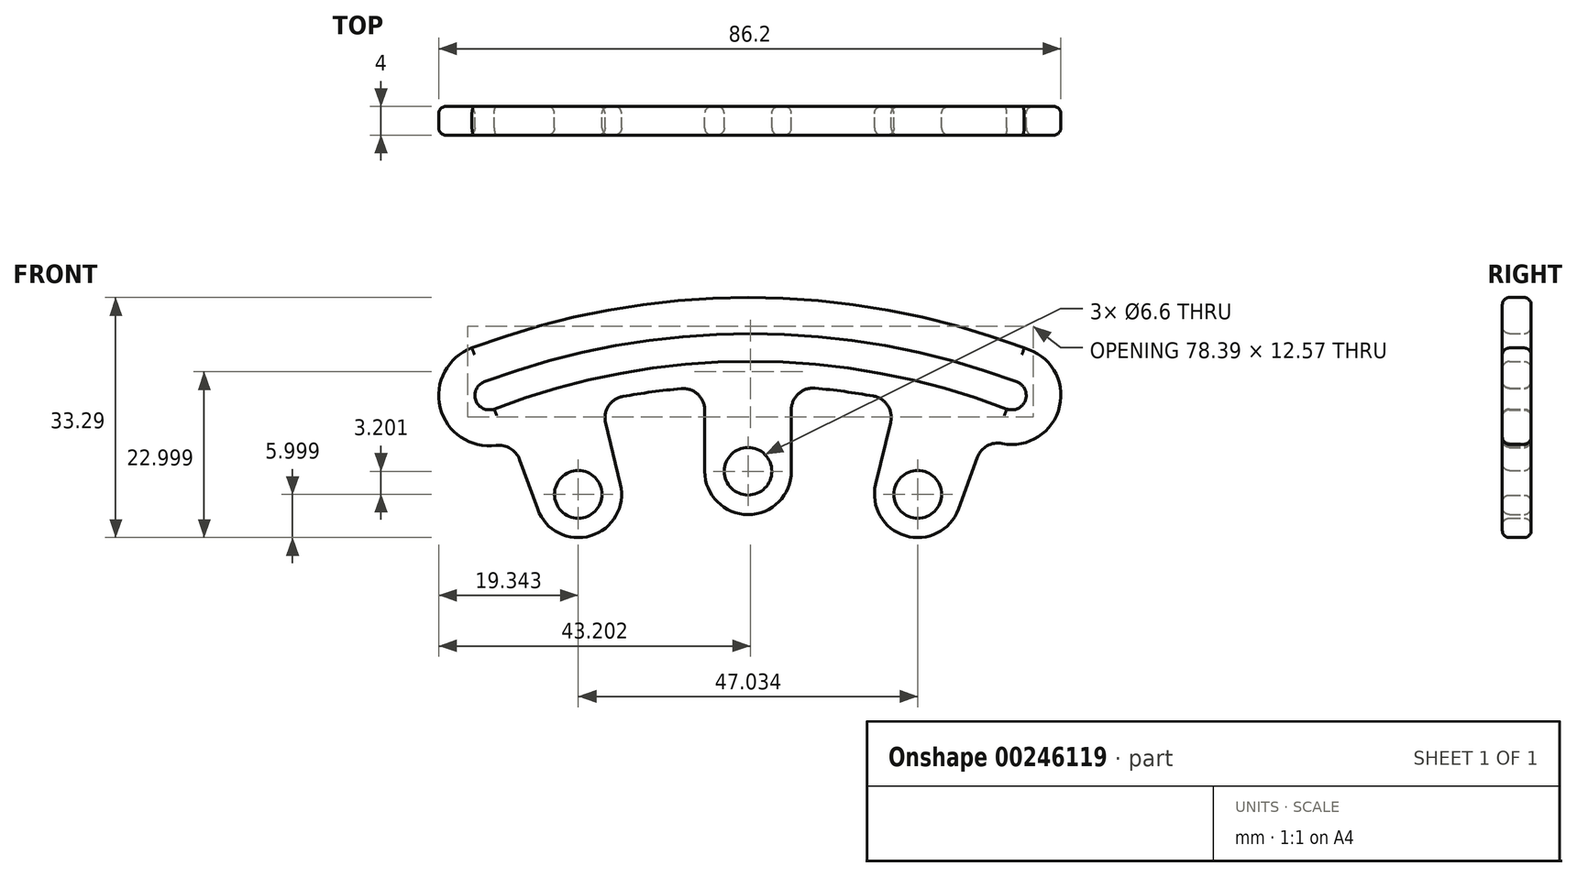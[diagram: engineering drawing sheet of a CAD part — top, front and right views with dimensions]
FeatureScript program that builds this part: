
annotation { "Feature Type Name" : "Feature", "Feature Type Description" : "" }
export const myFeature = defineFeature(function(context is Context, id is Id, definition is map)
    precondition{}
    {
        {
            var Q0;
            Q0=qCreatedBy(makeId("Front.planeOp"),FACE);
            var sketch = newSketch(context, id + "F0", { "sketchPlane" : qUnion([Q0])});
            skLineSegment(sketch, "E0", {"start": v(0, 0) * mm, "end": v(0, 189.24) * mm, "construction": true});
            skCircle(sketch, "E1", {"center": v(0, 88) * mm, "radius": 3.3 * mm});
            skCircle(sketch, "E2", {"center": v(23.52, 84.8) * mm, "radius": 3.3 * mm});
            skCircle(sketch, "E3", {"center": v(-23.52, 84.8) * mm, "radius": 3.3 * mm});
            skLineSegment(sketch, "E4", {"start": v(0, 0) * mm, "end": v(23.52, 84.8) * mm, "construction": true});
            skLineSegment(sketch, "E5", {"start": v(0, 0) * mm, "end": v(-23.52, 84.8) * mm, "construction": true});
            skArc(sketch, "E6", {"start": v(23.52, 84.8) * mm, "mid": v(0, 88) * mm, "end": v(-23.52, 84.8) * mm, "construction": true});
            skCircle(sketch, "E7", {"center": v(-23.52, 84.8) * mm, "radius": 6 * mm, "construction": true});
            skCircle(sketch, "E8", {"center": v(0, 88) * mm, "radius": 6 * mm, "construction": true});
            skCircle(sketch, "E9", {"center": v(23.52, 84.8) * mm, "radius": 6 * mm, "construction": true});
            skLineSegment(sketch, "E10", {"start": v(-23.52, 84.8) * mm, "end": v(23.52, 84.8) * mm, "construction": true});
            skLineSegment(sketch, "E11", {"start": v(-23.52, 84.8) * mm, "end": v(-17.68, 86.2) * mm, "construction": true});
            skLineSegment(sketch, "E12", {"start": v(0, 88) * mm, "end": v(69.3, 88) * mm, "construction": true});
            skLineSegment(sketch, "E13", {"start": v(69.3, 88) * mm, "end": v(69.3, 0) * mm, "construction": true});
            skLineSegment(sketch, "E14", {"start": v(0, 88) * mm, "end": v(6, 88) * mm, "construction": true});
            skLineSegment(sketch, "E15", {"start": v(6, 88) * mm, "end": v(6, 96.53) * mm});
            skLineSegment(sketch, "E16", {"start": v(0, 88) * mm, "end": v(-6, 88) * mm, "construction": true});
            skLineSegment(sketch, "E17", {"start": v(-6, 88) * mm, "end": v(-6, 96.47) * mm});
            skLineSegment(sketch, "E18", {"start": v(-23.52, 84.8) * mm, "end": v(-17.52, 84.8) * mm});
            skLineSegment(sketch, "E19", {"start": v(-17.68, 86.2) * mm, "end": v(-19.73, 94.72) * mm});
            skLineSegment(sketch, "E20", {"start": v(23.52, 84.8) * mm, "end": v(17.68, 86.2) * mm});
            skLineSegment(sketch, "E21", {"start": v(17.68, 86.2) * mm, "end": v(19.75, 94.78) * mm});
            skLineSegment(sketch, "E22", {"start": v(-35.17, 96.63) * mm, "end": v(35.86, 96.63) * mm, "construction": true});
            skArc(sketch, "E23", {"start": v(35.86, 96.63) * mm, "mid": v(0.34, 103.22) * mm, "end": v(-35.17, 96.63) * mm});
            skArc(sketch, "E24", {"start": v(-36.54, 100.4) * mm, "mid": v(-37.74, 97.83) * mm, "end": v(-35.17, 96.63) * mm});
            skArc(sketch, "E25", {"start": v(35.86, 96.63) * mm, "mid": v(38.42, 97.83) * mm, "end": v(37.22, 100.4) * mm});
            skArc(sketch, "E26", {"start": v(37.22, 100.4) * mm, "mid": v(0.34, 107.08) * mm, "end": v(-36.54, 100.4) * mm});
            skCircle(sketch, "E27", {"center": v(-35.86, 98.51) * mm, "radius": 3 * mm, "construction": true});
            skCircle(sketch, "E28", {"center": v(36.54, 98.51) * mm, "radius": 3 * mm, "construction": true});
            skLineSegment(sketch, "E29", {"start": v(-36.88, 101.33) * mm, "end": v(37.57, 101.33) * mm, "construction": true});
            skLineSegment(sketch, "E30", {"start": v(37.57, 101.33) * mm, "end": v(35.51, 95.7) * mm, "construction": true});
            skLineSegment(sketch, "E31", {"start": v(35.51, 95.7) * mm, "end": v(-34.83, 95.7) * mm, "construction": true});
            skArc(sketch, "E32", {"start": v(36.54, 98.51) * mm, "mid": v(0.34, 105.05) * mm, "end": v(-35.86, 98.51) * mm, "construction": true});
            skLineSegment(sketch, "E33", {"start": v(-38.25, 105.1) * mm, "end": v(38.25, 105.1) * mm, "construction": true});
            skLineSegment(sketch, "E34", {"start": v(-34.15, 93.81) * mm, "end": v(-34.15, 93.81) * mm, "construction": true});
            skArc(sketch, "E35", {"start": v(38.25, 105.1) * mm, "mid": v(0, 112.1) * mm, "end": v(-38.25, 105.1) * mm});
            skLineSegment(sketch, "E36", {"start": v(-23.52, 84.8) * mm, "end": v(-29.16, 82.75) * mm, "construction": true});
            skArc(sketch, "E37", {"start": v(-38.25, 105.1) * mm, "mid": v(-42.65, 96.83) * mm, "end": v(-34.9, 91.58) * mm});
            skArc(sketch, "E38", {"start": v(-9.28, 99.46) * mm, "mid": v(-13.32, 99) * mm, "end": v(-17.34, 98.37) * mm});
            skArc(sketch, "E39", {"start": v(17.35, 98.43) * mm, "mid": v(13.33, 99.06) * mm, "end": v(9.28, 99.52) * mm});
            skPoint(sketch, "E40.visualSharp", {"position": v(-20.47, 97.77) * mm});
            skArc(sketch, "E40.filletArc", {"start": v(-17.34, 98.37) * mm, "mid": v(-19.33, 97.06) * mm, "end": v(-19.73, 94.72) * mm});
            skPoint(sketch, "E41.visualSharp", {"position": v(-6, 99.7) * mm});
            skArc(sketch, "E41.filletArc", {"start": v(-6, 96.47) * mm, "mid": v(-6.98, 98.69) * mm, "end": v(-9.28, 99.46) * mm});
            skPoint(sketch, "E42.visualSharp", {"position": v(6, 99.77) * mm});
            skArc(sketch, "E42.filletArc", {"start": v(9.28, 99.52) * mm, "mid": v(6.98, 98.75) * mm, "end": v(6, 96.53) * mm});
            skPoint(sketch, "E43.visualSharp", {"position": v(20.48, 97.83) * mm});
            skArc(sketch, "E43.filletArc", {"start": v(19.75, 94.78) * mm, "mid": v(19.34, 97.12) * mm, "end": v(17.35, 98.43) * mm});
            skArc(sketch, "E44", {"start": v(-29.16, 82.75) * mm, "mid": v(-21.79, 79.05) * mm, "end": v(-17.68, 86.2) * mm});
            skArc(sketch, "E45", {"start": v(-6, 88) * mm, "mid": v(0, 82) * mm, "end": v(6, 88) * mm});
            skLineSegment(sketch, "E46", {"start": v(23.52, 84.8) * mm, "end": v(29.16, 82.75) * mm, "construction": true});
            skLineSegment(sketch, "E47", {"start": v(29.16, 82.75) * mm, "end": v(31.77, 89.94) * mm});
            skArc(sketch, "E48", {"start": v(35.19, 91.85) * mm, "mid": v(43.16, 96.98) * mm, "end": v(38.25, 105.1) * mm});
            skArc(sketch, "E49.filletArc", {"start": v(35.19, 91.85) * mm, "mid": v(33.12, 91.53) * mm, "end": v(31.77, 89.94) * mm});
            skLineSegment(sketch, "E50", {"start": v(-29.16, 82.75) * mm, "end": v(-31.66, 89.63) * mm});
            skArc(sketch, "E51.filletArc", {"start": v(-31.66, 89.63) * mm, "mid": v(-32.93, 91.18) * mm, "end": v(-34.9, 91.58) * mm});
            skArc(sketch, "E52", {"start": v(17.68, 86.2) * mm, "mid": v(21.79, 79.05) * mm, "end": v(29.16, 82.75) * mm});
            skSolve(sketch);
        }
        {
            var Q0;
            Q0 = qSketchRegion(id + "F0", true);
            extrude(context, id + "F1", {"entities" : qUnion([Q0]), "depth" : 4 * mm});
        }
        {
            var Q0;
            Q0=makeQuery(id+"F1.opExtrude","CAP_EDGE",EDGE,{"disambiguationData":[OSD([sQuery(id+"F0.wireOp",EDGE,"E35")])],"isStart":false});
            var Q1;
            Q1=makeQuery(id+"F1.opExtrude","CAP_FACE",FACE,{"disambiguationData":[OSD([sQuery(id+"F0.wireOp",EDGE,"E1"),sQuery(id+"F0.wireOp",EDGE,"E2"),sQuery(id+"F0.wireOp",EDGE,"E3"),sQuery(id+"F0.wireOp",EDGE,"E15"),sQuery(id+"F0.wireOp",EDGE,"E17"),sQuery(id+"F0.wireOp",EDGE,"E19"),sQuery(id+"F0.wireOp",EDGE,"E21"),sQuery(id+"F0.wireOp",EDGE,"E23"),sQuery(id+"F0.wireOp",EDGE,"E24"),sQuery(id+"F0.wireOp",EDGE,"E25"),sQuery(id+"F0.wireOp",EDGE,"E26"),sQuery(id+"F0.wireOp",EDGE,"E35"),sQuery(id+"F0.wireOp",EDGE,"E37"),sQuery(id+"F0.wireOp",EDGE,"E38"),sQuery(id+"F0.wireOp",EDGE,"E39"),sQuery(id+"F0.wireOp",EDGE,"E40.filletArc"),sQuery(id+"F0.wireOp",EDGE,"E41.filletArc"),sQuery(id+"F0.wireOp",EDGE,"E42.filletArc"),sQuery(id+"F0.wireOp",EDGE,"E43.filletArc"),sQuery(id+"F0.wireOp",EDGE,"E44"),sQuery(id+"F0.wireOp",EDGE,"E45"),sQuery(id+"F0.wireOp",EDGE,"E47"),sQuery(id+"F0.wireOp",EDGE,"E48"),sQuery(id+"F0.wireOp",EDGE,"E49.filletArc"),sQuery(id+"F0.wireOp",EDGE,"E50"),sQuery(id+"F0.wireOp",EDGE,"E51.filletArc"),sQuery(id+"F0.wireOp",EDGE,"E52")])],"isStart":false});
            var Q2;
            Q2=makeQuery(id+"F1.opExtrude","CAP_FACE",FACE,{"disambiguationData":[OSD([sQuery(id+"F0.wireOp",EDGE,"E1"),sQuery(id+"F0.wireOp",EDGE,"E2"),sQuery(id+"F0.wireOp",EDGE,"E3"),sQuery(id+"F0.wireOp",EDGE,"E15"),sQuery(id+"F0.wireOp",EDGE,"E17"),sQuery(id+"F0.wireOp",EDGE,"E19"),sQuery(id+"F0.wireOp",EDGE,"E21"),sQuery(id+"F0.wireOp",EDGE,"E23"),sQuery(id+"F0.wireOp",EDGE,"E24"),sQuery(id+"F0.wireOp",EDGE,"E25"),sQuery(id+"F0.wireOp",EDGE,"E26"),sQuery(id+"F0.wireOp",EDGE,"E35"),sQuery(id+"F0.wireOp",EDGE,"E37"),sQuery(id+"F0.wireOp",EDGE,"E38"),sQuery(id+"F0.wireOp",EDGE,"E39"),sQuery(id+"F0.wireOp",EDGE,"E40.filletArc"),sQuery(id+"F0.wireOp",EDGE,"E41.filletArc"),sQuery(id+"F0.wireOp",EDGE,"E42.filletArc"),sQuery(id+"F0.wireOp",EDGE,"E43.filletArc"),sQuery(id+"F0.wireOp",EDGE,"E44"),sQuery(id+"F0.wireOp",EDGE,"E45"),sQuery(id+"F0.wireOp",EDGE,"E47"),sQuery(id+"F0.wireOp",EDGE,"E48"),sQuery(id+"F0.wireOp",EDGE,"E49.filletArc"),sQuery(id+"F0.wireOp",EDGE,"E50"),sQuery(id+"F0.wireOp",EDGE,"E51.filletArc"),sQuery(id+"F0.wireOp",EDGE,"E52")])],"isStart":true});
            fillet(context, id + "F2", {"entities" : qUnion([Q0, Q1, Q2]), "radius" : 1 * mm, "tangentPropagation" : true, "allowEdgeOverflow" : false});
        }
    });
